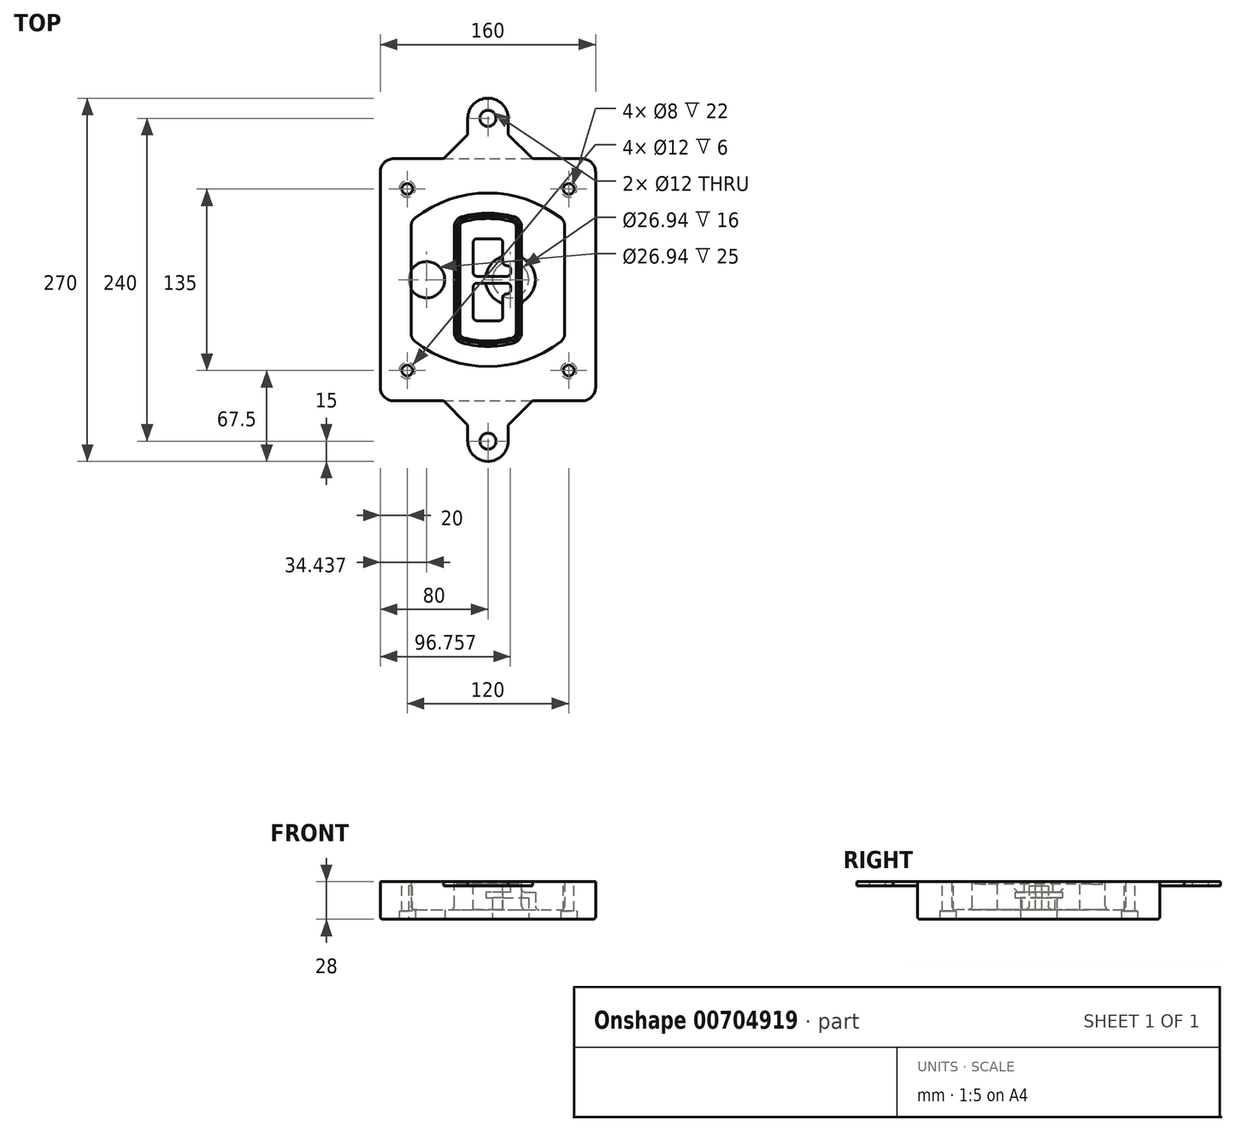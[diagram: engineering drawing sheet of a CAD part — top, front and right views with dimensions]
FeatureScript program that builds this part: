
annotation { "Feature Type Name" : "Feature", "Feature Type Description" : "" }
export const myFeature = defineFeature(function(context is Context, id is Id, definition is map)
    precondition{}
    {
        {
            var Q0;
            Q0=qCreatedBy(makeId("Top.planeOp"),FACE);
            var sketch = newSketch(context, id + "F0", { "sketchPlane" : qUnion([Q0])});
            skPoint(sketch, "E0.rect.middle", {"position": v(0, 0) * mm});
            skLineSegment(sketch, "E1.bottom", {"start": v(-70, -90) * mm, "end": v(70, -90) * mm});
            skLineSegment(sketch, "E1.top", {"start": v(-70, 90) * mm, "end": v(70, 90) * mm});
            skLineSegment(sketch, "E1.left", {"start": v(-80, -80) * mm, "end": v(-80, 80) * mm});
            skLineSegment(sketch, "E1.right", {"start": v(80, -80) * mm, "end": v(80, 80) * mm});
            skLineSegment(sketch, "E2", {"start": v(-80, 90) * mm, "end": v(80, -90) * mm, "construction": true});
            skLineSegment(sketch, "E3", {"start": v(80, 90) * mm, "end": v(-80, -90) * mm, "construction": true});
            skCircle(sketch, "E4", {"center": v(-60, 67.5) * mm, "radius": 4 * mm});
            skCircle(sketch, "E5", {"center": v(60, 67.5) * mm, "radius": 4 * mm});
            skCircle(sketch, "E6", {"center": v(60, -67.5) * mm, "radius": 4 * mm});
            skCircle(sketch, "E7", {"center": v(-60, -67.5) * mm, "radius": 4 * mm});
            skLineSegment(sketch, "E8", {"start": v(-60, 67.5) * mm, "end": v(60, 67.5) * mm, "construction": true});
            skLineSegment(sketch, "E9", {"start": v(60, 67.5) * mm, "end": v(60, -67.5) * mm, "construction": true});
            skLineSegment(sketch, "E10", {"start": v(60, -67.5) * mm, "end": v(-60, -67.5) * mm, "construction": true});
            skLineSegment(sketch, "E11", {"start": v(-60, -67.5) * mm, "end": v(-60, 67.5) * mm, "construction": true});
            skLineSegment(sketch, "E12", {"start": v(-60, 40.3) * mm, "end": v(-60, -40.3) * mm});
            skLineSegment(sketch, "E13", {"start": v(60, 40.3) * mm, "end": v(60, -40.3) * mm});
            skArc(sketch, "E14", {"start": v(56.15, 48.18) * mm, "mid": v(0, 67.5) * mm, "end": v(-56.15, 48.18) * mm});
            skArc(sketch, "E15", {"start": v(-56.15, -48.18) * mm, "mid": v(0, -67.5) * mm, "end": v(56.15, -48.18) * mm});
            skLineSegment(sketch, "E16", {"start": v(-60, 0) * mm, "end": v(60, 0) * mm, "construction": true});
            skPoint(sketch, "E17.visualSharp", {"position": v(-60, -45) * mm});
            skArc(sketch, "E17.filletArc", {"start": v(-60, -40.3) * mm, "mid": v(-58.99, -44.68) * mm, "end": v(-56.15, -48.18) * mm});
            skPoint(sketch, "E18.visualSharp", {"position": v(-60, 45) * mm});
            skArc(sketch, "E18.filletArc", {"start": v(-56.15, 48.18) * mm, "mid": v(-58.99, 44.68) * mm, "end": v(-60, 40.3) * mm});
            skPoint(sketch, "E19.visualSharp", {"position": v(60, 45) * mm});
            skArc(sketch, "E19.filletArc", {"start": v(60, 40.3) * mm, "mid": v(58.99, 44.68) * mm, "end": v(56.15, 48.18) * mm});
            skPoint(sketch, "E20.visualSharp", {"position": v(60, -45) * mm});
            skArc(sketch, "E20.filletArc", {"start": v(56.15, -48.18) * mm, "mid": v(58.99, -44.68) * mm, "end": v(60, -40.3) * mm});
            skPoint(sketch, "E21.visualSharp", {"position": v(-80, 90) * mm});
            skArc(sketch, "E21.filletArc", {"start": v(-70, 90) * mm, "mid": v(-77.07, 87.07) * mm, "end": v(-80, 80) * mm});
            skPoint(sketch, "E22.visualSharp", {"position": v(80, 90) * mm});
            skArc(sketch, "E22.filletArc", {"start": v(80, 80) * mm, "mid": v(77.07, 87.07) * mm, "end": v(70, 90) * mm});
            skPoint(sketch, "E23.visualSharp", {"position": v(80, -90) * mm});
            skArc(sketch, "E23.filletArc", {"start": v(70, -90) * mm, "mid": v(77.07, -87.07) * mm, "end": v(80, -80) * mm});
            skPoint(sketch, "E24.visualSharp", {"position": v(-80, -90) * mm});
            skArc(sketch, "E24.filletArc", {"start": v(-80, -80) * mm, "mid": v(-77.07, -87.07) * mm, "end": v(-70, -90) * mm});
            skArc(sketch, "E25.0", {"start": v(57, 40.3) * mm, "mid": v(56.3, 43.36) * mm, "end": v(54.3, 45.81) * mm});
            skLineSegment(sketch, "E25.1", {"start": v(57, 40.3) * mm, "end": v(57, -40.3) * mm});
            skArc(sketch, "E25.2", {"start": v(54.3, -45.81) * mm, "mid": v(56.3, -43.36) * mm, "end": v(57, -40.3) * mm});
            skArc(sketch, "E25.3", {"start": v(-54.3, -45.81) * mm, "mid": v(0, -64.5) * mm, "end": v(54.3, -45.81) * mm});
            skArc(sketch, "E25.4", {"start": v(-57, -40.3) * mm, "mid": v(-56.3, -43.36) * mm, "end": v(-54.3, -45.81) * mm});
            skArc(sketch, "E25.5", {"start": v(54.3, 45.81) * mm, "mid": v(0, 64.5) * mm, "end": v(-54.3, 45.81) * mm});
            skLineSegment(sketch, "E25.6", {"start": v(-57, 40.3) * mm, "end": v(-57, -40.3) * mm});
            skArc(sketch, "E25.7", {"start": v(-54.3, 45.81) * mm, "mid": v(-56.3, 43.36) * mm, "end": v(-57, 40.3) * mm});
            skArc(sketch, "E26.0", {"start": v(-58.62, 51.33) * mm, "mid": v(-62.58, 46.43) * mm, "end": v(-64, 40.3) * mm});
            skArc(sketch, "E26.1", {"start": v(58.62, 51.33) * mm, "mid": v(0, 71.5) * mm, "end": v(-58.62, 51.33) * mm});
            skArc(sketch, "E26.2", {"start": v(64, 40.3) * mm, "mid": v(62.58, 46.43) * mm, "end": v(58.62, 51.33) * mm});
            skLineSegment(sketch, "E26.3", {"start": v(64, 40.3) * mm, "end": v(64, -40.3) * mm});
            skArc(sketch, "E26.4", {"start": v(58.62, -51.33) * mm, "mid": v(62.58, -46.43) * mm, "end": v(64, -40.3) * mm});
            skLineSegment(sketch, "E26.5", {"start": v(-64, 40.3) * mm, "end": v(-64, -40.3) * mm});
            skArc(sketch, "E26.6", {"start": v(-58.62, -51.33) * mm, "mid": v(0, -71.5) * mm, "end": v(58.62, -51.33) * mm});
            skArc(sketch, "E26.7", {"start": v(-64, -40.3) * mm, "mid": v(-62.58, -46.43) * mm, "end": v(-58.62, -51.33) * mm});
            skSolve(sketch);
        }
        {
            var Q0;
            Q0=makeQuery(id+"F0.imprint","IMPRINT",FACE,{"disambiguationData":[TD([[makeQuery(id+"F0.imprint","IMPRINT",EDGE,{"derivedFrom":sQuery(id+"F0.wireOp",EDGE,"E1.bottom")}),1.0]])]});
            var Q1;
            Q1=makeQuery(id+"F0.imprint","IMPRINT",FACE,{"disambiguationData":[TD([[makeQuery(id+"F0.imprint","IMPRINT",EDGE,{"derivedFrom":sQuery(id+"F0.wireOp",EDGE,"E12")}),1.0]])]});
            var Q2;
            Q2=makeQuery(id+"F0.imprint","IMPRINT",FACE,{"disambiguationData":[TD([[makeQuery(id+"F0.imprint","IMPRINT",EDGE,{"derivedFrom":sQuery(id+"F0.wireOp",EDGE,"E25.0")}),1.0]])]});
            var Q3;
            Q3=makeQuery(id+"F0.imprint","IMPRINT",FACE,{"disambiguationData":[TD([[makeQuery(id+"F0.imprint","IMPRINT",EDGE,{"derivedFrom":sQuery(id+"F0.wireOp",EDGE,"E12")}),-1.0]])]});
            extrude(context, id + "F1", {"entities" : qUnion([Q0, Q1, Q2, Q3]), "oppositeDirection" : true, "depth" : 25 * mm});
        }
        {
            var Q0;
            Q0=makeQuery(id+"F0.imprint","IMPRINT",FACE,{"disambiguationData":[TD([[makeQuery(id+"F0.imprint","IMPRINT",EDGE,{"derivedFrom":sQuery(id+"F0.wireOp",EDGE,"E12")}),1.0]])]});
            extrude(context, id + "F2", {"entities" : qUnion([Q0]), "operationType" : NewBodyOperationType.ADD, "depth" : 3 * mm});
        }
        {
            var Q0;
            Q0=makeQuery(id+"F0.imprint","IMPRINT",FACE,{"disambiguationData":[TD([[makeQuery(id+"F0.imprint","IMPRINT",EDGE,{"derivedFrom":sQuery(id+"F0.wireOp",EDGE,"E25.0")}),1.0]])]});
            extrude(context, id + "F3", {"entities" : qUnion([Q0]), "operationType" : NewBodyOperationType.REMOVE, "oppositeDirection" : true, "depth" : 18 * mm});
        }
        {
            var Q0;
            Q0=makeQuery(id+"F2.opExtrude","CAP_FACE",FACE,{"disambiguationData":[OSD([sQuery(id+"F0.wireOp",EDGE,"E12"),sQuery(id+"F0.wireOp",EDGE,"E13"),sQuery(id+"F0.wireOp",EDGE,"E14"),sQuery(id+"F0.wireOp",EDGE,"E15"),sQuery(id+"F0.wireOp",EDGE,"E17.filletArc"),sQuery(id+"F0.wireOp",EDGE,"E18.filletArc"),sQuery(id+"F0.wireOp",EDGE,"E19.filletArc"),sQuery(id+"F0.wireOp",EDGE,"E20.filletArc"),sQuery(id+"F0.wireOp",EDGE,"E25.0"),sQuery(id+"F0.wireOp",EDGE,"E25.1"),sQuery(id+"F0.wireOp",EDGE,"E25.2"),sQuery(id+"F0.wireOp",EDGE,"E25.3"),sQuery(id+"F0.wireOp",EDGE,"E25.4"),sQuery(id+"F0.wireOp",EDGE,"E25.5"),sQuery(id+"F0.wireOp",EDGE,"E25.6"),sQuery(id+"F0.wireOp",EDGE,"E25.7")])],"isStart":false});
            var sketch = newSketch(context, id + "F4", { "sketchPlane" : qUnion([Q0])});
            skArc(sketch, "E27.0", {"start": v(-19.08, -46.97) * mm, "mid": v(0, -49.5) * mm, "end": v(19.08, -46.97) * mm});
            skArc(sketch, "E28.0", {"start": v(19.08, 46.97) * mm, "mid": v(0, 49.5) * mm, "end": v(-19.08, 46.97) * mm});
            skLineSegment(sketch, "E29", {"start": v(-25, 39.25) * mm, "end": v(-25, -39.25) * mm});
            skLineSegment(sketch, "E30", {"start": v(25, 39.25) * mm, "end": v(25, -39.25) * mm});
            skLineSegment(sketch, "E31", {"start": v(-25, 45.1) * mm, "end": v(25, 45.1) * mm, "construction": true});
            skLineSegment(sketch, "E32", {"start": v(-25, -45.1) * mm, "end": v(25, -45.1) * mm, "construction": true});
            skPoint(sketch, "E33.visualSharp", {"position": v(-25, 45.1) * mm});
            skArc(sketch, "E33.filletArc", {"start": v(-19.08, 46.97) * mm, "mid": v(-23.35, 44.11) * mm, "end": v(-25, 39.25) * mm});
            skPoint(sketch, "E34.visualSharp", {"position": v(25, 45.1) * mm});
            skArc(sketch, "E34.filletArc", {"start": v(25, 39.25) * mm, "mid": v(23.35, 44.11) * mm, "end": v(19.08, 46.97) * mm});
            skPoint(sketch, "E35.visualSharp", {"position": v(25, -45.1) * mm});
            skArc(sketch, "E35.filletArc", {"start": v(19.08, -46.97) * mm, "mid": v(23.35, -44.11) * mm, "end": v(25, -39.25) * mm});
            skPoint(sketch, "E36.visualSharp", {"position": v(-25, -45.1) * mm});
            skArc(sketch, "E36.filletArc", {"start": v(-25, -39.25) * mm, "mid": v(-23.35, -44.11) * mm, "end": v(-19.08, -46.97) * mm});
            skArc(sketch, "E37.0", {"start": v(54.3, 45.81) * mm, "mid": v(0, 64.5) * mm, "end": v(-54.3, 45.81) * mm});
            skArc(sketch, "E37.1", {"start": v(-54.3, 45.81) * mm, "mid": v(-56.3, 43.36) * mm, "end": v(-57, 40.3) * mm});
            skLineSegment(sketch, "E37.2", {"start": v(-57, 40.3) * mm, "end": v(-57, -40.3) * mm});
            skArc(sketch, "E37.3", {"start": v(-57, -40.3) * mm, "mid": v(-56.3, -43.36) * mm, "end": v(-54.3, -45.81) * mm});
            skArc(sketch, "E37.4", {"start": v(-54.3, -45.81) * mm, "mid": v(0, -64.5) * mm, "end": v(54.3, -45.81) * mm});
            skArc(sketch, "E37.5", {"start": v(54.3, -45.81) * mm, "mid": v(56.3, -43.36) * mm, "end": v(57, -40.3) * mm});
            skLineSegment(sketch, "E37.6", {"start": v(57, 40.3) * mm, "end": v(57, -40.3) * mm});
            skArc(sketch, "E37.7", {"start": v(57, 40.3) * mm, "mid": v(56.3, 43.36) * mm, "end": v(54.3, 45.81) * mm});
            skLineSegment(sketch, "E38.0", {"start": v(23, 39.25) * mm, "end": v(23, -39.25) * mm});
            skArc(sketch, "E38.1", {"start": v(18.56, -45.04) * mm, "mid": v(21.76, -42.9) * mm, "end": v(23, -39.25) * mm});
            skArc(sketch, "E38.2", {"start": v(-18.56, -45.04) * mm, "mid": v(0, -47.5) * mm, "end": v(18.56, -45.04) * mm});
            skArc(sketch, "E38.3", {"start": v(-23, -39.25) * mm, "mid": v(-21.76, -42.9) * mm, "end": v(-18.56, -45.04) * mm});
            skLineSegment(sketch, "E38.4", {"start": v(-23, 39.25) * mm, "end": v(-23, -39.25) * mm});
            skArc(sketch, "E38.5", {"start": v(23, 39.25) * mm, "mid": v(21.76, 42.9) * mm, "end": v(18.56, 45.04) * mm});
            skArc(sketch, "E38.6", {"start": v(-18.56, 45.04) * mm, "mid": v(-21.76, 42.9) * mm, "end": v(-23, 39.25) * mm});
            skArc(sketch, "E38.7", {"start": v(18.56, 45.04) * mm, "mid": v(0, 47.5) * mm, "end": v(-18.56, 45.04) * mm});
            skArc(sketch, "E39.0", {"start": v(21, 39.25) * mm, "mid": v(20.18, 41.68) * mm, "end": v(18.04, 43.1) * mm});
            skLineSegment(sketch, "E39.1", {"start": v(21, 39.25) * mm, "end": v(21, -39.25) * mm});
            skArc(sketch, "E39.2", {"start": v(18.04, -43.1) * mm, "mid": v(20.18, -41.68) * mm, "end": v(21, -39.25) * mm});
            skArc(sketch, "E39.3", {"start": v(-18.04, -43.1) * mm, "mid": v(0, -45.5) * mm, "end": v(18.04, -43.1) * mm});
            skArc(sketch, "E39.4", {"start": v(-21, -39.25) * mm, "mid": v(-20.18, -41.68) * mm, "end": v(-18.04, -43.1) * mm});
            skArc(sketch, "E39.5", {"start": v(18.04, 43.1) * mm, "mid": v(0, 45.5) * mm, "end": v(-18.04, 43.1) * mm});
            skLineSegment(sketch, "E39.6", {"start": v(-21, 39.25) * mm, "end": v(-21, -39.25) * mm});
            skArc(sketch, "E39.7", {"start": v(-18.04, 43.1) * mm, "mid": v(-20.18, 41.68) * mm, "end": v(-21, 39.25) * mm});
            skLineSegment(sketch, "E40", {"start": v(-25, 0) * mm, "end": v(25, 0) * mm, "construction": true});
            skLineSegment(sketch, "E41", {"start": v(-11, 5.5) * mm, "end": v(-11, 27.5) * mm});
            skLineSegment(sketch, "E42", {"start": v(-8, 30.5) * mm, "end": v(8, 30.5) * mm});
            skLineSegment(sketch, "E43", {"start": v(11, 27.5) * mm, "end": v(11, 13.5) * mm});
            skLineSegment(sketch, "E44", {"start": v(14, 10.5) * mm, "end": v(14, 10.5) * mm});
            skLineSegment(sketch, "E45", {"start": v(17, 7.5) * mm, "end": v(17, 5.5) * mm});
            skLineSegment(sketch, "E46", {"start": v(14, 2.5) * mm, "end": v(-8, 2.5) * mm});
            skPoint(sketch, "E47.visualSharp", {"position": v(-11, 30.5) * mm});
            skArc(sketch, "E47.filletArc", {"start": v(-8, 30.5) * mm, "mid": v(-10.12, 29.62) * mm, "end": v(-11, 27.5) * mm});
            skPoint(sketch, "E48.visualSharp", {"position": v(11, 30.5) * mm});
            skArc(sketch, "E48.filletArc", {"start": v(11, 27.5) * mm, "mid": v(10.12, 29.62) * mm, "end": v(8, 30.5) * mm});
            skPoint(sketch, "E49.visualSharp", {"position": v(11, 10.5) * mm});
            skArc(sketch, "E49.filletArc", {"start": v(11, 13.5) * mm, "mid": v(11.88, 11.38) * mm, "end": v(14, 10.5) * mm});
            skPoint(sketch, "E50.visualSharp", {"position": v(17, 10.5) * mm});
            skArc(sketch, "E50.filletArc", {"start": v(17, 7.5) * mm, "mid": v(16.12, 9.62) * mm, "end": v(14, 10.5) * mm});
            skPoint(sketch, "E51.visualSharp", {"position": v(17, 2.5) * mm});
            skArc(sketch, "E51.filletArc", {"start": v(14, 2.5) * mm, "mid": v(16.12, 3.38) * mm, "end": v(17, 5.5) * mm});
            skPoint(sketch, "E52.visualSharp", {"position": v(-11, 2.5) * mm});
            skArc(sketch, "E52.filletArc", {"start": v(-11, 5.5) * mm, "mid": v(-10.12, 3.38) * mm, "end": v(-8, 2.5) * mm});
            skLineSegment(sketch, "E53.0.MirrorCS", {"start": v(14, -2.5) * mm, "end": v(-8, -2.5) * mm});
            skArc(sketch, "E54.0.MirrorCS", {"start": v(-11, -5.5) * mm, "mid": v(-10.12, -3.38) * mm, "end": v(-8, -2.5) * mm});
            skLineSegment(sketch, "E55.0.MirrorCS", {"start": v(-11, -5.5) * mm, "end": v(-11, -27.5) * mm});
            skArc(sketch, "E56.0.MirrorCS", {"start": v(-8, -30.5) * mm, "mid": v(-10.12, -29.62) * mm, "end": v(-11, -27.5) * mm});
            skLineSegment(sketch, "E57.0.MirrorCS", {"start": v(-8, -30.5) * mm, "end": v(8, -30.5) * mm});
            skArc(sketch, "E58.0.MirrorCS", {"start": v(11, -27.5) * mm, "mid": v(10.12, -29.62) * mm, "end": v(8, -30.5) * mm});
            skLineSegment(sketch, "E59.0.MirrorCS", {"start": v(11, -27.5) * mm, "end": v(11, -13.5) * mm});
            skArc(sketch, "E60.0.MirrorCS", {"start": v(11, -13.5) * mm, "mid": v(11.88, -11.38) * mm, "end": v(14, -10.5) * mm});
            skArc(sketch, "E61.0.MirrorCS", {"start": v(17, -7.5) * mm, "mid": v(16.12, -9.62) * mm, "end": v(14, -10.5) * mm});
            skLineSegment(sketch, "E62.0.MirrorCS", {"start": v(17, -7.5) * mm, "end": v(17, -5.5) * mm});
            skArc(sketch, "E63.0.MirrorCS", {"start": v(14, -2.5) * mm, "mid": v(16.12, -3.38) * mm, "end": v(17, -5.5) * mm});
            skSolve(sketch);
        }
        {
            var Q0;
            Q0=makeQuery(id+"F4.imprint","IMPRINT",FACE,{"disambiguationData":[TD([[makeQuery(id+"F4.imprint","IMPRINT",EDGE,{"derivedFrom":sQuery(id+"F4.wireOp",EDGE,"E27.0")}),1.0]])]});
            var Q1;
            Q1=makeQuery(id+"F4.imprint","IMPRINT",FACE,{"disambiguationData":[TD([[makeQuery(id+"F4.imprint","IMPRINT",EDGE,{"derivedFrom":sQuery(id+"F4.wireOp",EDGE,"E38.0")}),-1.0]])]});
            var Q2;
            Q2=makeQuery(id+"F4.imprint","IMPRINT",FACE,{"disambiguationData":[TD([[makeQuery(id+"F4.imprint","IMPRINT",EDGE,{"derivedFrom":sQuery(id+"F4.wireOp",EDGE,"E39.0")}),1.0]])]});
            extrude(context, id + "F5", {"entities" : qUnion([Q0, Q1, Q2]), "operationType" : NewBodyOperationType.ADD, "endBound" : BoundingType.UP_TO_NEXT, "oppositeDirection" : true, "depth" : 25 * mm});
        }
        {
            var Q0;
            Q0=makeQuery(id+"F4.imprint","IMPRINT",FACE,{"disambiguationData":[TD([[makeQuery(id+"F4.imprint","IMPRINT",EDGE,{"derivedFrom":sQuery(id+"F4.wireOp",EDGE,"E38.0")}),-1.0]])]});
            extrude(context, id + "F6", {"entities" : qUnion([Q0]), "operationType" : NewBodyOperationType.REMOVE, "oppositeDirection" : true, "depth" : 2 * mm});
        }
        {
            var Q0;
            Q0=makeQuery(id+"F1.opExtrude","CAP_FACE",FACE,{"disambiguationData":[OSD([sQuery(id+"F0.wireOp",EDGE,"E1.bottom"),sQuery(id+"F0.wireOp",EDGE,"E1.top"),sQuery(id+"F0.wireOp",EDGE,"E1.left"),sQuery(id+"F0.wireOp",EDGE,"E1.right"),sQuery(id+"F0.wireOp",EDGE,"E4"),sQuery(id+"F0.wireOp",EDGE,"E5"),sQuery(id+"F0.wireOp",EDGE,"E6"),sQuery(id+"F0.wireOp",EDGE,"E7"),sQuery(id+"F0.wireOp",EDGE,"E21.filletArc"),sQuery(id+"F0.wireOp",EDGE,"E22.filletArc"),sQuery(id+"F0.wireOp",EDGE,"E23.filletArc"),sQuery(id+"F0.wireOp",EDGE,"E24.filletArc")])],"isStart":false});
            var sketch = newSketch(context, id + "F7", { "sketchPlane" : qUnion([Q0])});
            skCircle(sketch, "E64", {"center": v(16.76, 0) * mm, "radius": 13.47 * mm});
            skCircle(sketch, "E65", {"center": v(-45.56, 0) * mm, "radius": 13.47 * mm});
            skLineSegment(sketch, "E66", {"start": v(80, 0) * mm, "end": v(-80, 0) * mm});
            skCircle(sketch, "E67", {"center": v(16.76, 0) * mm, "radius": 18.47 * mm});
            skCircle(sketch, "E68", {"center": v(60, -67.5) * mm, "radius": 6 * mm});
            skCircle(sketch, "E69", {"center": v(-60, -67.5) * mm, "radius": 6 * mm});
            skCircle(sketch, "E70", {"center": v(-60, 67.5) * mm, "radius": 6 * mm});
            skCircle(sketch, "E71", {"center": v(60, 67.5) * mm, "radius": 6 * mm});
            skSolve(sketch);
        }
        {
            var Q0;
            {var subQ1=sQuery(id+"F7.wireOp",EDGE,"E66");var subQ4=sQuery(id+"F7.wireOp",EDGE,"E64");var subQ6=makeQuery(id+"F7.imprint","INTERSECT",VERTEX,{"disambiguationData":[OD(0.0)],"derivedFrom":[subQ4,subQ1]});Q0=makeQuery(id+"F7.imprint","IMPRINT",FACE,{"disambiguationData":[TD([[makeQuery(id+"F7.imprint","IMPRINT",EDGE,{"disambiguationData":[TD([[subQ6,-1.0]])],"derivedFrom":subQ4}),-1.0]])]});}
            var Q1;
            {var subQ0=sQuery(id+"F7.wireOp",EDGE,"E66");var subQ1=sQuery(id+"F7.wireOp",EDGE,"E64");var subQ3=makeQuery(id+"F7.imprint","INTERSECT",VERTEX,{"disambiguationData":[OD(0.0)],"derivedFrom":[subQ1,subQ0]});Q1=makeQuery(id+"F7.imprint","IMPRINT",FACE,{"disambiguationData":[TD([[makeQuery(id+"F7.imprint","IMPRINT",EDGE,{"disambiguationData":[TD([[subQ3,-1.0]])],"derivedFrom":subQ1}),1.0]])]});}
            var Q2;
            {var subQ0=sQuery(id+"F7.wireOp",EDGE,"E66");var subQ1=sQuery(id+"F7.wireOp",EDGE,"E64");var subQ3=makeQuery(id+"F7.imprint","INTERSECT",VERTEX,{"disambiguationData":[OD(0.0)],"derivedFrom":[subQ1,subQ0]});Q2=makeQuery(id+"F7.imprint","IMPRINT",FACE,{"disambiguationData":[TD([[makeQuery(id+"F7.imprint","IMPRINT",EDGE,{"disambiguationData":[TD([[subQ3,1.0]])],"derivedFrom":subQ1}),1.0]])]});}
            var Q3;
            {var subQ1=sQuery(id+"F7.wireOp",EDGE,"E66");var subQ4=sQuery(id+"F7.wireOp",EDGE,"E64");var subQ6=makeQuery(id+"F7.imprint","INTERSECT",VERTEX,{"disambiguationData":[OD(0.0)],"derivedFrom":[subQ4,subQ1]});Q3=makeQuery(id+"F7.imprint","IMPRINT",FACE,{"disambiguationData":[TD([[makeQuery(id+"F7.imprint","IMPRINT",EDGE,{"disambiguationData":[TD([[subQ6,1.0]])],"derivedFrom":subQ4}),-1.0]])]});}
            extrude(context, id + "F8", {"entities" : qUnion([Q0, Q1, Q2, Q3]), "operationType" : NewBodyOperationType.ADD, "oppositeDirection" : true, "depth" : 20 * mm});
        }
        {
            var Q0;
            {var subQ0=sQuery(id+"F7.wireOp",EDGE,"E66");var subQ1=sQuery(id+"F7.wireOp",EDGE,"E64");var subQ3=makeQuery(id+"F7.imprint","INTERSECT",VERTEX,{"disambiguationData":[OD(0.0)],"derivedFrom":[subQ1,subQ0]});Q0=makeQuery(id+"F7.imprint","IMPRINT",FACE,{"disambiguationData":[TD([[makeQuery(id+"F7.imprint","IMPRINT",EDGE,{"disambiguationData":[TD([[subQ3,-1.0]])],"derivedFrom":subQ1}),1.0]])]});}
            var Q1;
            {var subQ0=sQuery(id+"F7.wireOp",EDGE,"E66");var subQ1=sQuery(id+"F7.wireOp",EDGE,"E64");var subQ3=makeQuery(id+"F7.imprint","INTERSECT",VERTEX,{"disambiguationData":[OD(0.0)],"derivedFrom":[subQ1,subQ0]});Q1=makeQuery(id+"F7.imprint","IMPRINT",FACE,{"disambiguationData":[TD([[makeQuery(id+"F7.imprint","IMPRINT",EDGE,{"disambiguationData":[TD([[subQ3,1.0]])],"derivedFrom":subQ1}),1.0]])]});}
            extrude(context, id + "F9", {"entities" : qUnion([Q0, Q1]), "operationType" : NewBodyOperationType.REMOVE, "oppositeDirection" : true, "depth" : 16 * mm});
        }
        {
            var Q0;
            {var subQ0=sQuery(id+"F7.wireOp",EDGE,"E66");var subQ1=sQuery(id+"F7.wireOp",EDGE,"E65");var subQ3=makeQuery(id+"F7.imprint","INTERSECT",VERTEX,{"disambiguationData":[OD(0.0)],"derivedFrom":[subQ1,subQ0]});Q0=makeQuery(id+"F7.imprint","IMPRINT",FACE,{"disambiguationData":[TD([[makeQuery(id+"F7.imprint","IMPRINT",EDGE,{"disambiguationData":[TD([[subQ3,-1.0]])],"derivedFrom":subQ1}),1.0]])]});}
            var Q1;
            {var subQ0=sQuery(id+"F7.wireOp",EDGE,"E66");var subQ1=sQuery(id+"F7.wireOp",EDGE,"E65");var subQ3=makeQuery(id+"F7.imprint","INTERSECT",VERTEX,{"disambiguationData":[OD(0.0)],"derivedFrom":[subQ1,subQ0]});Q1=makeQuery(id+"F7.imprint","IMPRINT",FACE,{"disambiguationData":[TD([[makeQuery(id+"F7.imprint","IMPRINT",EDGE,{"disambiguationData":[TD([[subQ3,1.0]])],"derivedFrom":subQ1}),1.0]])]});}
            extrude(context, id + "F10", {"entities" : qUnion([Q0, Q1]), "operationType" : NewBodyOperationType.REMOVE, "oppositeDirection" : true, "depth" : 25 * mm});
        }
        {
            var Q0;
            Q0=makeQuery(id+"F7.imprint","IMPRINT",FACE,{"disambiguationData":[TD([[makeQuery(id+"F7.imprint","IMPRINT",EDGE,{"derivedFrom":sQuery(id+"F7.wireOp",EDGE,"E68")}),1.0]])]});
            var Q1;
            Q1=makeQuery(id+"F7.imprint","IMPRINT",FACE,{"disambiguationData":[TD([[makeQuery(id+"F7.imprint","IMPRINT",EDGE,{"derivedFrom":makeQuery(id+"F1.opExtrude","CAP_EDGE",EDGE,{"disambiguationData":[OSD([sQuery(id+"F0.wireOp",EDGE,"E5")])],"isStart":false})}),-1.0]])]});
            var Q2;
            Q2=makeQuery(id+"F7.imprint","IMPRINT",FACE,{"disambiguationData":[TD([[makeQuery(id+"F7.imprint","IMPRINT",EDGE,{"derivedFrom":sQuery(id+"F7.wireOp",EDGE,"E69")}),1.0]])]});
            var Q3;
            Q3=makeQuery(id+"F7.imprint","IMPRINT",FACE,{"disambiguationData":[TD([[makeQuery(id+"F7.imprint","IMPRINT",EDGE,{"derivedFrom":makeQuery(id+"F1.opExtrude","CAP_EDGE",EDGE,{"disambiguationData":[OSD([sQuery(id+"F0.wireOp",EDGE,"E4")])],"isStart":false})}),-1.0]])]});
            var Q4;
            Q4=makeQuery(id+"F7.imprint","IMPRINT",FACE,{"disambiguationData":[TD([[makeQuery(id+"F7.imprint","IMPRINT",EDGE,{"derivedFrom":sQuery(id+"F7.wireOp",EDGE,"E70")}),1.0]])]});
            var Q5;
            Q5=makeQuery(id+"F7.imprint","IMPRINT",FACE,{"disambiguationData":[TD([[makeQuery(id+"F7.imprint","IMPRINT",EDGE,{"derivedFrom":makeQuery(id+"F1.opExtrude","CAP_EDGE",EDGE,{"disambiguationData":[OSD([sQuery(id+"F0.wireOp",EDGE,"E7")])],"isStart":false})}),-1.0]])]});
            var Q6;
            Q6=makeQuery(id+"F7.imprint","IMPRINT",FACE,{"disambiguationData":[TD([[makeQuery(id+"F7.imprint","IMPRINT",EDGE,{"derivedFrom":sQuery(id+"F7.wireOp",EDGE,"E71")}),1.0]])]});
            var Q7;
            Q7=makeQuery(id+"F7.imprint","IMPRINT",FACE,{"disambiguationData":[TD([[makeQuery(id+"F7.imprint","IMPRINT",EDGE,{"derivedFrom":makeQuery(id+"F1.opExtrude","CAP_EDGE",EDGE,{"disambiguationData":[OSD([sQuery(id+"F0.wireOp",EDGE,"E6")])],"isStart":false})}),-1.0]])]});
            extrude(context, id + "F11", {"entities" : qUnion([Q0, Q1, Q2, Q3, Q4, Q5, Q6, Q7]), "operationType" : NewBodyOperationType.REMOVE, "oppositeDirection" : true, "depth" : 6 * mm});
        }
        {
            var Q0;
            Q0=makeQuery(id+"F9.boolean.opBoolean","COPY",FACE,{"derivedFrom":makeQuery(id+"F9.opExtrude","CAP_FACE",FACE,{"disambiguationData":[OSD([sQuery(id+"F7.wireOp",EDGE,"E64")])],"isStart":false})});
            var sketch = newSketch(context, id + "F12", { "sketchPlane" : qUnion([Q0])});
            skArc(sketch, "E72.0", {"start": v(11, 17.55) * mm, "mid": v(2.57, 11.82) * mm, "end": v(-1.54, 2.5) * mm});
            skArc(sketch, "E72.1", {"start": v(-1.54, -2.5) * mm, "mid": v(2.57, -11.82) * mm, "end": v(11, -17.55) * mm});
            skLineSegment(sketch, "E73", {"start": v(-1.54, -2.5) * mm, "end": v(14, -2.5) * mm});
            skLineSegment(sketch, "E74.0", {"start": v(14, 2.5) * mm, "end": v(-1.54, 2.5) * mm});
            skArc(sketch, "E74.1", {"start": v(14, 2.5) * mm, "mid": v(16.12, 3.38) * mm, "end": v(17, 5.5) * mm});
            skLineSegment(sketch, "E74.2", {"start": v(17, 7.5) * mm, "end": v(17, 5.5) * mm});
            skArc(sketch, "E74.3", {"start": v(17, 7.5) * mm, "mid": v(16.12, 9.62) * mm, "end": v(14, 10.5) * mm});
            skArc(sketch, "E74.4", {"start": v(11, 13.5) * mm, "mid": v(11.88, 11.38) * mm, "end": v(14, 10.5) * mm});
            skLineSegment(sketch, "E74.5", {"start": v(11, 17.55) * mm, "end": v(11, 13.5) * mm});
            skLineSegment(sketch, "E74.7", {"start": v(14, -2.5) * mm, "end": v(-1.54, -2.5) * mm});
            skArc(sketch, "E74.8", {"start": v(14, -2.5) * mm, "mid": v(16.12, -3.38) * mm, "end": v(17, -5.5) * mm});
            skLineSegment(sketch, "E74.9", {"start": v(17, -7.5) * mm, "end": v(17, -5.5) * mm});
            skArc(sketch, "E74.10", {"start": v(17, -7.5) * mm, "mid": v(16.12, -9.62) * mm, "end": v(14, -10.5) * mm});
            skArc(sketch, "E74.11", {"start": v(11, -13.5) * mm, "mid": v(11.88, -11.38) * mm, "end": v(14, -10.5) * mm});
            skLineSegment(sketch, "E74.12", {"start": v(11, -17.55) * mm, "end": v(11, -13.5) * mm});
            skPoint(sketch, "E75.orphan", {"position": v(11, -27.5) * mm});
            skPoint(sketch, "E76.orphan", {"position": v(-8, -2.5) * mm});
            skPoint(sketch, "E77.orphan", {"position": v(-8, 2.5) * mm});
            skPoint(sketch, "E78.orphan", {"position": v(11, 27.5) * mm});
            skSolve(sketch);
        }
        {
            var Q0;
            {var subQ7=sQuery(id+"F12.wireOp",EDGE,"E72.0");var subQ14=sQuery(id+"F12.wireOp",EDGE,"E72.1");var subQ16=sQuery(id+"F12.wireOp",EDGE,"E74.1");var subQ18=sQuery(id+"F12.wireOp",EDGE,"E74.8");Q0=qUnion([makeQuery(id+"F12.imprint","IMPRINT",FACE,{"disambiguationData":[TD([[makeQuery(id+"F12.imprint","IMPRINT",EDGE,{"derivedFrom":subQ7}),1.0]])]}),makeQuery(id+"F12.imprint","IMPRINT",FACE,{"disambiguationData":[TD([[makeQuery(id+"F12.imprint","IMPRINT",EDGE,{"derivedFrom":subQ14}),1.0]])]}),makeQuery(id+"F12.imprint","IMPRINT",FACE,{"disambiguationData":[TD([[makeQuery(id+"F12.imprint","IMPRINT",EDGE,{"derivedFrom":subQ16}),1.0]])]}),makeQuery(id+"F12.imprint","IMPRINT",FACE,{"disambiguationData":[TD([[makeQuery(id+"F12.imprint","IMPRINT",EDGE,{"derivedFrom":subQ18}),-1.0]])]})]);}
            var Q1;
            Q1=makeQuery(id+"F5.boolean.opBoolean","SPLIT",FACE,{"disambiguationData":[TD([makeQuery(id+"F5.opExtrude","SWEPT_FACE",FACE,{"disambiguationData":[OSD([sQuery(id+"F4.wireOp",EDGE,"E41")])]})])],"derivedFrom":makeQuery(id+"F3.boolean.opBoolean","COPY",FACE,{"derivedFrom":makeQuery(id+"F3.opExtrude","CAP_FACE",FACE,{"disambiguationData":[OSD([sQuery(id+"F0.wireOp",EDGE,"E25.0"),sQuery(id+"F0.wireOp",EDGE,"E25.1"),sQuery(id+"F0.wireOp",EDGE,"E25.2"),sQuery(id+"F0.wireOp",EDGE,"E25.3"),sQuery(id+"F0.wireOp",EDGE,"E25.4"),sQuery(id+"F0.wireOp",EDGE,"E25.5"),sQuery(id+"F0.wireOp",EDGE,"E25.6"),sQuery(id+"F0.wireOp",EDGE,"E25.7")])],"isStart":false})})});
            extrude(context, id + "F13", {"entities" : qUnion([Q0]), "operationType" : NewBodyOperationType.REMOVE, "endBound" : BoundingType.UP_TO_SURFACE, "endBoundEntityFace" : qUnion([Q1]), "depth" : 25 * mm});
        }
        {
            var Q0;
            Q0=makeQuery(id+"F3.boolean.opBoolean","COPY",EDGE,{"derivedFrom":makeQuery(id+"F3.opExtrude","CAP_EDGE",EDGE,{"disambiguationData":[OSD([sQuery(id+"F0.wireOp",EDGE,"E25.6")])],"isStart":false})});
            var Q1;
            Q1=makeQuery(id+"F8.boolean.opBoolean","INTERSECT",EDGE,{"derivedFrom":[makeQuery(id+"F5.opExtrude","SWEPT_FACE",FACE,{"disambiguationData":[OSD([sQuery(id+"F4.wireOp",EDGE,"E30")])]}),makeQuery(id+"F8.opExtrude","CAP_FACE",FACE,{"disambiguationData":[OSD([sQuery(id+"F7.wireOp",EDGE,"E67")])],"isStart":false})]});
            var Q2;
            Q2=makeQuery(id+"F8.boolean.opBoolean","INTERSECT",EDGE,{"disambiguationData":[OD(1.0)],"derivedFrom":[makeQuery(id+"F5.opExtrude","SWEPT_FACE",FACE,{"disambiguationData":[OSD([sQuery(id+"F4.wireOp",EDGE,"E30")])]}),makeQuery(id+"F8.opExtrude","SWEPT_FACE",FACE,{"disambiguationData":[OSD([sQuery(id+"F7.wireOp",EDGE,"E67")])]})]});
            var Q3;
            {var subQ0=sQuery(id+"F4.wireOp",EDGE,"E30");Q3=makeQuery(id+"F8.boolean.opBoolean","SPLIT",EDGE,{"disambiguationData":[TD([makeQuery(id+"F5.opExtrude","SWEPT_FACE",FACE,{"disambiguationData":[OSD([sQuery(id+"F4.wireOp",EDGE,"E35.filletArc")])]})])],"derivedFrom":makeQuery(id+"F5.opExtrude","CAP_EDGE",EDGE,{"disambiguationData":[OSD([subQ0])],"isStart":false})});}
            var Q4;
            {var subQ0=sQuery(id+"F0.wireOp",EDGE,"E25.7");var subQ1=sQuery(id+"F0.wireOp",EDGE,"E25.1");var subQ2=sQuery(id+"F0.wireOp",EDGE,"E25.6");var subQ3=sQuery(id+"F0.wireOp",EDGE,"E25.5");var subQ4=sQuery(id+"F0.wireOp",EDGE,"E25.4");var subQ5=sQuery(id+"F0.wireOp",EDGE,"E25.0");var subQ6=sQuery(id+"F0.wireOp",EDGE,"E25.2");var subQ7=sQuery(id+"F0.wireOp",EDGE,"E25.3");Q4=makeQuery(id+"F8.boolean.opBoolean","INTERSECT",EDGE,{"derivedFrom":[makeQuery(id+"F5.boolean.opBoolean","SPLIT",FACE,{"disambiguationData":[TD([makeQuery(id+"F2.opExtrude","SWEPT_FACE",FACE,{"disambiguationData":[OSD([subQ5])]})])],"derivedFrom":makeQuery(id+"F3.boolean.opBoolean","COPY",FACE,{"derivedFrom":makeQuery(id+"F3.opExtrude","CAP_FACE",FACE,{"disambiguationData":[OSD([subQ5,subQ1,subQ6,subQ7,subQ4,subQ3,subQ2,subQ0])],"isStart":false})})}),makeQuery(id+"F8.opExtrude","SWEPT_FACE",FACE,{"disambiguationData":[OSD([sQuery(id+"F7.wireOp",EDGE,"E67")])]})]});}
            var Q5;
            Q5=makeQuery(id+"F8.boolean.opBoolean","INTERSECT",EDGE,{"disambiguationData":[OD(0.0)],"derivedFrom":[makeQuery(id+"F5.opExtrude","SWEPT_FACE",FACE,{"disambiguationData":[OSD([sQuery(id+"F4.wireOp",EDGE,"E30")])]}),makeQuery(id+"F8.opExtrude","SWEPT_FACE",FACE,{"disambiguationData":[OSD([sQuery(id+"F7.wireOp",EDGE,"E67")])]})]});
            fillet(context, id + "F14", {"entities" : qUnion([Q0, Q1, Q2, Q3, Q4, Q5]), "radius" : 3 * mm, "tangentPropagation" : true, "allowEdgeOverflow" : false});
        }
        {
            var Q0;
            Q0=makeQuery(id+"F1.opExtrude","CAP_EDGE",EDGE,{"disambiguationData":[OSD([sQuery(id+"F0.wireOp",EDGE,"E1.bottom")])],"isStart":false});
            fillet(context, id + "F15", {"entities" : qUnion([Q0]), "radius" : 2 * mm, "tangentPropagation" : true, "allowEdgeOverflow" : false});
        }
        {
            var Q0;
            {var subQ0=sQuery(id+"F0.wireOp",EDGE,"E21.filletArc");var subQ1=sQuery(id+"F0.wireOp",EDGE,"E7");var subQ2=sQuery(id+"F0.wireOp",EDGE,"E6");var subQ3=sQuery(id+"F0.wireOp",EDGE,"E5");var subQ4=sQuery(id+"F0.wireOp",EDGE,"E4");var subQ5=sQuery(id+"F0.wireOp",EDGE,"E22.filletArc");var subQ6=sQuery(id+"F0.wireOp",EDGE,"E1.bottom");var subQ7=sQuery(id+"F0.wireOp",EDGE,"E1.right");var subQ8=sQuery(id+"F0.wireOp",EDGE,"E1.top");var subQ9=sQuery(id+"F0.wireOp",EDGE,"E1.left");var subQ10=sQuery(id+"F0.wireOp",EDGE,"E23.filletArc");var subQ11=sQuery(id+"F0.wireOp",EDGE,"E24.filletArc");Q0=makeQuery(id+"F2.boolean.opBoolean","SPLIT",FACE,{"disambiguationData":[TD([makeQuery(id+"F1.opExtrude","SWEPT_FACE",FACE,{"disambiguationData":[OSD([subQ6])]})])],"derivedFrom":makeQuery(id+"F1.opExtrude","CAP_FACE",FACE,{"disambiguationData":[OSD([subQ6,subQ8,subQ9,subQ7,subQ4,subQ3,subQ2,subQ1,subQ0,subQ5,subQ10,subQ11])],"isStart":true})});}
            var sketch = newSketch(context, id + "F16", { "sketchPlane" : qUnion([Q0])});
            skLineSegment(sketch, "E79", {"start": v(-15, 108) * mm, "end": v(-15, 120) * mm});
            skLineSegment(sketch, "E80", {"start": v(15, 120) * mm, "end": v(15, 108) * mm});
            skArc(sketch, "E81", {"start": v(15, 120) * mm, "mid": v(0, 135) * mm, "end": v(-15, 120) * mm});
            skCircle(sketch, "E82", {"center": v(0, 120) * mm, "radius": 6 * mm});
            skLineSegment(sketch, "E83", {"start": v(-15, 108) * mm, "end": v(-33, 90) * mm});
            skLineSegment(sketch, "E84", {"start": v(15, 108) * mm, "end": v(33, 90) * mm});
            skLineSegment(sketch, "E85.MirrorCS", {"start": v(-15, -108) * mm, "end": v(-15, -120) * mm});
            skLineSegment(sketch, "E86.MirrorCS", {"start": v(15, -120) * mm, "end": v(15, -108) * mm});
            skLineSegment(sketch, "E87.MirrorCS", {"start": v(15, -108) * mm, "end": v(33, -90) * mm});
            skLineSegment(sketch, "E88.MirrorCS", {"start": v(-15, -108) * mm, "end": v(-33, -90) * mm});
            skCircle(sketch, "E89.MirrorC", {"center": v(0, -120) * mm, "radius": 6 * mm});
            skArc(sketch, "E90.MirrorCS", {"start": v(15, -120) * mm, "mid": v(0, -135) * mm, "end": v(-15, -120) * mm});
            skSolve(sketch);
        }
        {
            var Q0;
            Q0=makeQuery(id+"F16.imprint","IMPRINT",FACE,{"disambiguationData":[TD([[makeQuery(id+"F16.imprint","IMPRINT",EDGE,{"derivedFrom":sQuery(id+"F16.wireOp",EDGE,"E85.MirrorCS")}),1.0]])]});
            var Q1;
            Q1=makeQuery(id+"F16.imprint","IMPRINT",FACE,{"disambiguationData":[TD([[makeQuery(id+"F16.imprint","IMPRINT",EDGE,{"derivedFrom":sQuery(id+"F16.wireOp",EDGE,"E79")}),-1.0]])]});
            var Q2;
            Q2=makeQuery(id+"F16.imprint","IMPRINT",FACE,{"disambiguationData":[TD([[makeQuery(id+"F16.imprint","IMPRINT",EDGE,{"derivedFrom":makeQuery(id+"F1.opExtrude","CAP_EDGE",EDGE,{"disambiguationData":[OSD([sQuery(id+"F0.wireOp",EDGE,"E1.left")])],"isStart":true})}),-1.0]])]});
            var Q3;
            Q3=makeQuery(id+"F2.opExtrude","CAP_FACE",FACE,{"disambiguationData":[OSD([sQuery(id+"F0.wireOp",EDGE,"E12"),sQuery(id+"F0.wireOp",EDGE,"E13"),sQuery(id+"F0.wireOp",EDGE,"E14"),sQuery(id+"F0.wireOp",EDGE,"E15"),sQuery(id+"F0.wireOp",EDGE,"E17.filletArc"),sQuery(id+"F0.wireOp",EDGE,"E18.filletArc"),sQuery(id+"F0.wireOp",EDGE,"E19.filletArc"),sQuery(id+"F0.wireOp",EDGE,"E20.filletArc"),sQuery(id+"F0.wireOp",EDGE,"E25.0"),sQuery(id+"F0.wireOp",EDGE,"E25.1"),sQuery(id+"F0.wireOp",EDGE,"E25.2"),sQuery(id+"F0.wireOp",EDGE,"E25.3"),sQuery(id+"F0.wireOp",EDGE,"E25.4"),sQuery(id+"F0.wireOp",EDGE,"E25.5"),sQuery(id+"F0.wireOp",EDGE,"E25.6"),sQuery(id+"F0.wireOp",EDGE,"E25.7")])],"isStart":false});
            extrude(context, id + "F17", {"entities" : qUnion([Q0, Q1, Q2]), "operationType" : NewBodyOperationType.ADD, "endBound" : BoundingType.UP_TO_SURFACE, "depth" : 25 * mm, "endBoundEntityFace" : qUnion([Q3]), "offsetDistance" : 25 * mm});
        }
    });
